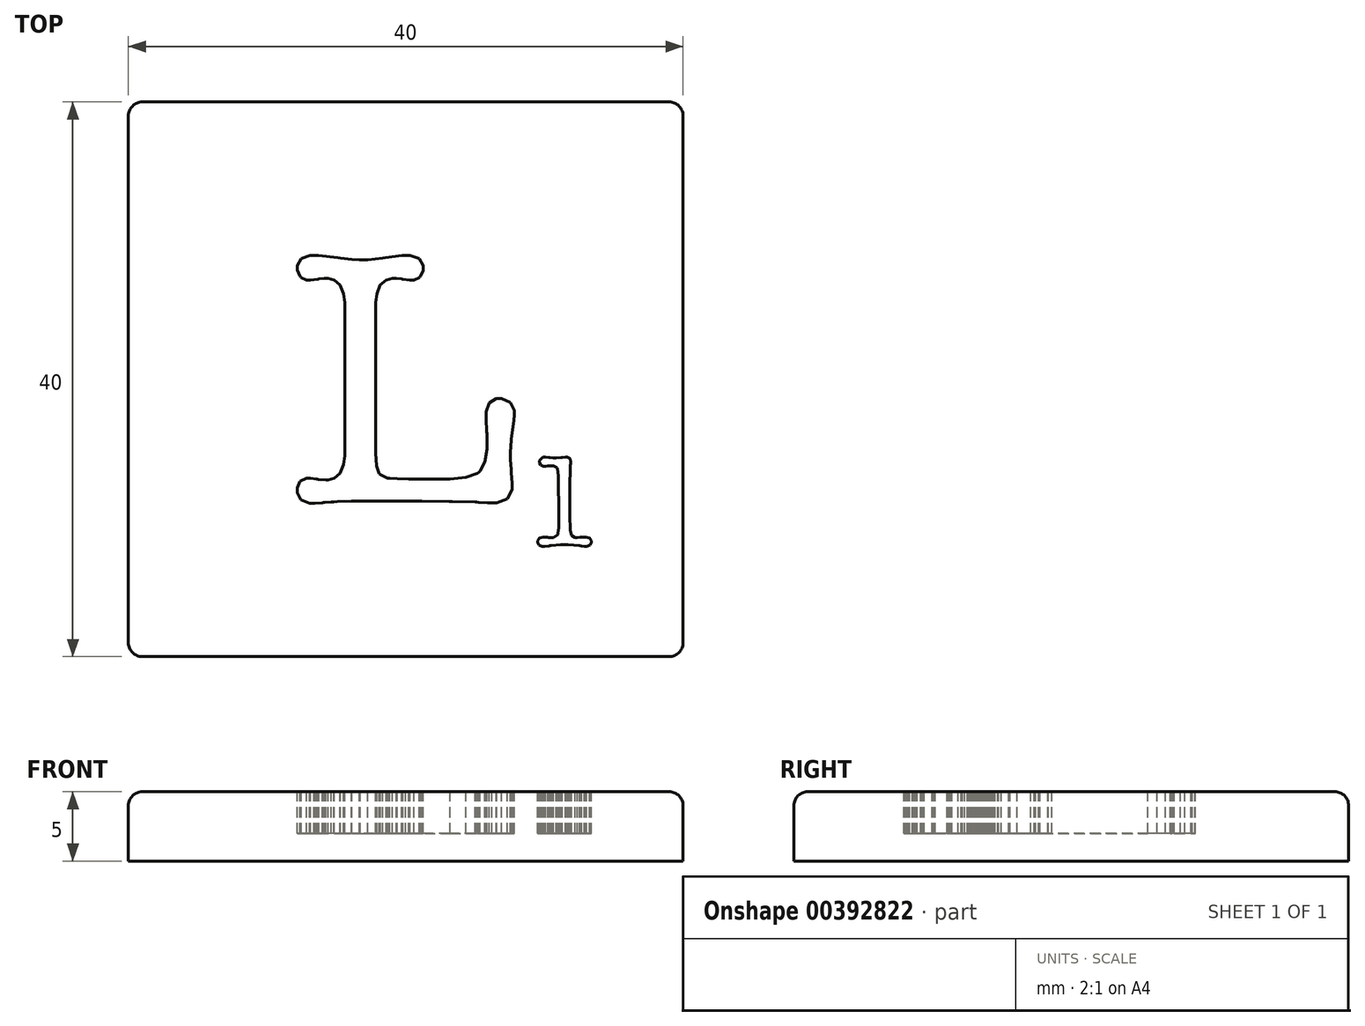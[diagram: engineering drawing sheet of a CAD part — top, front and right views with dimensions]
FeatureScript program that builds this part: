
annotation { "Feature Type Name" : "Feature", "Feature Type Description" : "" }
export const myFeature = defineFeature(function(context is Context, id is Id, definition is map)
    precondition{}
    {
        {
            var Q0;
            Q0=qCreatedBy(makeId("Top.planeOp"),FACE);
            var sketch = newSketch(context, id + "F0", { "sketchPlane" : qUnion([Q0])});
            skLineSegment(sketch, "E0.bottom", {"start": v(20, -20) * mm, "end": v(-20, -20) * mm});
            skLineSegment(sketch, "E0.top", {"start": v(20, 20) * mm, "end": v(-20, 20) * mm});
            skLineSegment(sketch, "E0.left", {"start": v(20, -20) * mm, "end": v(20, 20) * mm});
            skLineSegment(sketch, "E0.right", {"start": v(-20, -20) * mm, "end": v(-20, 20) * mm});
            skPoint(sketch, "E0.middle", {"position": v(0, 0) * mm});
            skSolve(sketch);
        }
        {
            var Q0;
            Q0=makeQuery(id+"F0.imprint","IMPRINT",FACE,{"disambiguationData":[TD([[makeQuery(id+"F0.imprint","IMPRINT",EDGE,{"derivedFrom":sQuery(id+"F0.wireOp",EDGE,"E0.bottom")}),-1.0]])]});
            extrude(context, id + "F1", {"entities" : qUnion([Q0]), "depth" : -5 * mm});
        }
        {
            var Q0;
            Q0=makeQuery(id+"F1.opExtrude","CAP_FACE",FACE,{"disambiguationData":[OSD([sQuery(id+"F0.wireOp",EDGE,"E0.bottom"),sQuery(id+"F0.wireOp",EDGE,"E0.top"),sQuery(id+"F0.wireOp",EDGE,"E0.left"),sQuery(id+"F0.wireOp",EDGE,"E0.right")])],"isStart":true});
            var Q1;
            Q1=makeQuery(id+"F1.opExtrude","SWEPT_EDGE",EDGE,{"disambiguationData":[OSD([sQuery(id+"F0.wireOp",EDGE,"E0.top"),sQuery(id+"F0.wireOp",EDGE,"E0.right")])]});
            var Q2;
            Q2=makeQuery(id+"F1.opExtrude","SWEPT_EDGE",EDGE,{"disambiguationData":[OSD([sQuery(id+"F0.wireOp",EDGE,"E0.top"),sQuery(id+"F0.wireOp",EDGE,"E0.left")])]});
            var Q3;
            Q3=makeQuery(id+"F1.opExtrude","SWEPT_EDGE",EDGE,{"disambiguationData":[OSD([sQuery(id+"F0.wireOp",EDGE,"E0.bottom"),sQuery(id+"F0.wireOp",EDGE,"E0.right")])]});
            var Q4;
            Q4=makeQuery(id+"F1.opExtrude","SWEPT_EDGE",EDGE,{"disambiguationData":[OSD([sQuery(id+"F0.wireOp",EDGE,"E0.bottom"),sQuery(id+"F0.wireOp",EDGE,"E0.left")])]});
            fillet(context, id + "F2", {"entities" : qUnion([Q0, Q1, Q2, Q3, Q4]), "radius" : 1 * mm, "tangentPropagation" : true, "allowEdgeOverflow" : false});
        }
        {
            var Q0;
            Q0=qCreatedBy(makeId("Top.planeOp"),FACE);
            var sketch = newSketch(context, id + "F3", { "sketchPlane" : qUnion([Q0])});
            skLineSegment(sketch, "E1", {"start": v(-2.17, -5) * mm, "end": v(-2.17, -5.31) * mm});
            skLineSegment(sketch, "E2", {"start": v(-2.17, -5.31) * mm, "end": v(-2.1, -6.24) * mm});
            skLineSegment(sketch, "E3", {"start": v(-2.1, -6.24) * mm, "end": v(-1.9, -6.8) * mm});
            skLineSegment(sketch, "E4", {"start": v(-1.9, -6.8) * mm, "end": v(-1.85, -6.85) * mm});
            skLineSegment(sketch, "E5", {"start": v(-1.85, -6.85) * mm, "end": v(-1.81, -6.9) * mm});
            skLineSegment(sketch, "E6", {"start": v(-1.81, -6.9) * mm, "end": v(-1.3, -7.13) * mm});
            skLineSegment(sketch, "E7", {"start": v(-1.3, -7.13) * mm, "end": v(-1.23, -7.14) * mm});
            skLineSegment(sketch, "E8", {"start": v(-1.23, -7.14) * mm, "end": v(-1.17, -7.15) * mm});
            skLineSegment(sketch, "E9", {"start": v(-1.17, -7.15) * mm, "end": v(-0.6, -7.18) * mm});
            skLineSegment(sketch, "E10", {"start": v(-0.6, -7.18) * mm, "end": v(0.22, -7.2) * mm});
            skLineSegment(sketch, "E11", {"start": v(0.22, -7.2) * mm, "end": v(0.5, -7.2) * mm});
            skLineSegment(sketch, "E12", {"start": v(0.5, -7.2) * mm, "end": v(2.83, -7.2) * mm});
            skLineSegment(sketch, "E13", {"start": v(2.83, -7.2) * mm, "end": v(3.21, -7.2) * mm});
            skLineSegment(sketch, "E14", {"start": v(3.21, -7.2) * mm, "end": v(4.35, -7.07) * mm});
            skLineSegment(sketch, "E15", {"start": v(4.35, -7.07) * mm, "end": v(5.16, -6.79) * mm});
            skLineSegment(sketch, "E16", {"start": v(5.16, -6.79) * mm, "end": v(5.27, -6.7) * mm});
            skLineSegment(sketch, "E17", {"start": v(5.27, -6.7) * mm, "end": v(5.37, -6.62) * mm});
            skLineSegment(sketch, "E18", {"start": v(5.37, -6.62) * mm, "end": v(5.72, -5.97) * mm});
            skLineSegment(sketch, "E19", {"start": v(5.72, -5.97) * mm, "end": v(5.87, -5.04) * mm});
            skLineSegment(sketch, "E20", {"start": v(5.87, -5.04) * mm, "end": v(5.87, -4.74) * mm});
            skLineSegment(sketch, "E21", {"start": v(5.87, -4.74) * mm, "end": v(5.87, -4.5) * mm});
            skLineSegment(sketch, "E22", {"start": v(5.87, -4.5) * mm, "end": v(5.85, -3.9) * mm});
            skLineSegment(sketch, "E23", {"start": v(5.85, -3.9) * mm, "end": v(5.85, -3.8) * mm});
            skLineSegment(sketch, "E24", {"start": v(5.85, -3.8) * mm, "end": v(5.84, -3.64) * mm});
            skLineSegment(sketch, "E25", {"start": v(5.84, -3.64) * mm, "end": v(5.8, -2.98) * mm});
            skLineSegment(sketch, "E26", {"start": v(5.8, -2.98) * mm, "end": v(5.8, -2.67) * mm});
            skLineSegment(sketch, "E27", {"start": v(5.8, -2.67) * mm, "end": v(5.8, -2.57) * mm});
            skLineSegment(sketch, "E28", {"start": v(5.8, -2.57) * mm, "end": v(5.8, -2.35) * mm});
            skLineSegment(sketch, "E29", {"start": v(5.8, -2.35) * mm, "end": v(6.03, -1.7) * mm});
            skLineSegment(sketch, "E30", {"start": v(6.03, -1.7) * mm, "end": v(6.55, -1.4) * mm});
            skLineSegment(sketch, "E31", {"start": v(6.55, -1.4) * mm, "end": v(6.72, -1.4) * mm});
            skLineSegment(sketch, "E32", {"start": v(6.72, -1.4) * mm, "end": v(6.93, -1.4) * mm});
            skLineSegment(sketch, "E33", {"start": v(6.93, -1.4) * mm, "end": v(7.55, -1.67) * mm});
            skLineSegment(sketch, "E34", {"start": v(7.55, -1.67) * mm, "end": v(7.83, -2.26) * mm});
            skLineSegment(sketch, "E35", {"start": v(7.83, -2.26) * mm, "end": v(7.83, -2.46) * mm});
            skLineSegment(sketch, "E36", {"start": v(7.83, -2.46) * mm, "end": v(7.83, -2.59) * mm});
            skLineSegment(sketch, "E37", {"start": v(7.83, -2.59) * mm, "end": v(7.8, -2.93) * mm});
            skLineSegment(sketch, "E38", {"start": v(7.8, -2.93) * mm, "end": v(7.8, -2.96) * mm});
            skLineSegment(sketch, "E39", {"start": v(7.8, -2.96) * mm, "end": v(7.62, -4.31) * mm});
            skLineSegment(sketch, "E40", {"start": v(7.62, -4.31) * mm, "end": v(7.6, -4.4) * mm});
            skLineSegment(sketch, "E41", {"start": v(7.6, -4.4) * mm, "end": v(7.54, -5.25) * mm});
            skLineSegment(sketch, "E42", {"start": v(7.54, -5.25) * mm, "end": v(7.54, -5.53) * mm});
            skLineSegment(sketch, "E43", {"start": v(7.54, -5.53) * mm, "end": v(7.54, -5.8) * mm});
            skLineSegment(sketch, "E44", {"start": v(7.54, -5.8) * mm, "end": v(7.6, -6.5) * mm});
            skLineSegment(sketch, "E45", {"start": v(7.6, -6.5) * mm, "end": v(7.6, -6.63) * mm});
            skLineSegment(sketch, "E46", {"start": v(7.6, -6.63) * mm, "end": v(7.62, -6.75) * mm});
            skLineSegment(sketch, "E47", {"start": v(7.62, -6.75) * mm, "end": v(7.67, -7.48) * mm});
            skLineSegment(sketch, "E48", {"start": v(7.67, -7.48) * mm, "end": v(7.67, -7.73) * mm});
            skLineSegment(sketch, "E49", {"start": v(7.67, -7.73) * mm, "end": v(7.67, -7.95) * mm});
            skLineSegment(sketch, "E50", {"start": v(7.67, -7.95) * mm, "end": v(7.34, -8.62) * mm});
            skLineSegment(sketch, "E51", {"start": v(7.34, -8.62) * mm, "end": v(6.58, -8.92) * mm});
            skLineSegment(sketch, "E52", {"start": v(6.58, -8.92) * mm, "end": v(6.32, -8.92) * mm});
            skLineSegment(sketch, "E53", {"start": v(6.32, -8.92) * mm, "end": v(6.21, -8.92) * mm});
            skLineSegment(sketch, "E54", {"start": v(6.21, -8.92) * mm, "end": v(5.89, -8.9) * mm});
            skLineSegment(sketch, "E55", {"start": v(5.89, -8.9) * mm, "end": v(5.27, -8.87) * mm});
            skLineSegment(sketch, "E56", {"start": v(5.27, -8.87) * mm, "end": v(5.1, -8.86) * mm});
            skLineSegment(sketch, "E57", {"start": v(5.1, -8.86) * mm, "end": v(5, -8.86) * mm});
            skLineSegment(sketch, "E58", {"start": v(5, -8.86) * mm, "end": v(3.37, -8.81) * mm});
            skLineSegment(sketch, "E59", {"start": v(3.37, -8.81) * mm, "end": v(3.15, -8.81) * mm});
            skLineSegment(sketch, "E60", {"start": v(3.15, -8.81) * mm, "end": v(1.16, -8.78) * mm});
            skLineSegment(sketch, "E61", {"start": v(1.16, -8.78) * mm, "end": v(-3.07, -8.78) * mm});
            skLineSegment(sketch, "E62", {"start": v(-3.07, -8.78) * mm, "end": v(-3.28, -8.78) * mm});
            skLineSegment(sketch, "E63", {"start": v(-3.28, -8.78) * mm, "end": v(-3.92, -8.8) * mm});
            skLineSegment(sketch, "E64", {"start": v(-3.92, -8.8) * mm, "end": v(-4.94, -8.83) * mm});
            skLineSegment(sketch, "E65", {"start": v(-4.94, -8.83) * mm, "end": v(-5.19, -8.84) * mm});
            skLineSegment(sketch, "E66", {"start": v(-5.19, -8.84) * mm, "end": v(-5.37, -8.84) * mm});
            skLineSegment(sketch, "E67", {"start": v(-5.37, -8.84) * mm, "end": v(-5.83, -8.88) * mm});
            skLineSegment(sketch, "E68", {"start": v(-5.83, -8.88) * mm, "end": v(-5.91, -8.9) * mm});
            skLineSegment(sketch, "E69", {"start": v(-5.91, -8.9) * mm, "end": v(-6, -8.9) * mm});
            skLineSegment(sketch, "E70", {"start": v(-6, -8.9) * mm, "end": v(-6.54, -8.94) * mm});
            skLineSegment(sketch, "E71", {"start": v(-6.54, -8.94) * mm, "end": v(-6.72, -8.94) * mm});
            skLineSegment(sketch, "E72", {"start": v(-6.72, -8.94) * mm, "end": v(-6.93, -8.94) * mm});
            skLineSegment(sketch, "E73", {"start": v(-6.93, -8.94) * mm, "end": v(-7.55, -8.7) * mm});
            skLineSegment(sketch, "E74", {"start": v(-7.55, -8.7) * mm, "end": v(-7.83, -8.17) * mm});
            skLineSegment(sketch, "E75", {"start": v(-7.83, -8.17) * mm, "end": v(-7.83, -8) * mm});
            skLineSegment(sketch, "E76", {"start": v(-7.83, -8) * mm, "end": v(-7.83, -7.83) * mm});
            skLineSegment(sketch, "E77", {"start": v(-7.83, -7.83) * mm, "end": v(-7.63, -7.35) * mm});
            skLineSegment(sketch, "E78", {"start": v(-7.63, -7.35) * mm, "end": v(-7.17, -7.14) * mm});
            skLineSegment(sketch, "E79", {"start": v(-7.17, -7.14) * mm, "end": v(-7.01, -7.14) * mm});
            skLineSegment(sketch, "E80", {"start": v(-7.01, -7.14) * mm, "end": v(-6.85, -7.14) * mm});
            skLineSegment(sketch, "E81", {"start": v(-6.85, -7.14) * mm, "end": v(-6.45, -7.2) * mm});
            skLineSegment(sketch, "E82", {"start": v(-6.45, -7.2) * mm, "end": v(-6.38, -7.2) * mm});
            skLineSegment(sketch, "E83", {"start": v(-6.38, -7.2) * mm, "end": v(-6.3, -7.22) * mm});
            skLineSegment(sketch, "E84", {"start": v(-6.3, -7.22) * mm, "end": v(-5.74, -7.28) * mm});
            skLineSegment(sketch, "E85", {"start": v(-5.74, -7.28) * mm, "end": v(-5.6, -7.28) * mm});
            skLineSegment(sketch, "E86", {"start": v(-5.6, -7.28) * mm, "end": v(-5.15, -7.15) * mm});
            skLineSegment(sketch, "E87", {"start": v(-5.15, -7.15) * mm, "end": v(-4.73, -6.78) * mm});
            skLineSegment(sketch, "E88", {"start": v(-4.73, -6.78) * mm, "end": v(-4.48, -6.16) * mm});
            skLineSegment(sketch, "E89", {"start": v(-4.48, -6.16) * mm, "end": v(-4.4, -5.5) * mm});
            skLineSegment(sketch, "E90", {"start": v(-4.4, -5.5) * mm, "end": v(-4.4, -5.3) * mm});
            skLineSegment(sketch, "E91", {"start": v(-4.4, -5.3) * mm, "end": v(-4.4, 5.32) * mm});
            skLineSegment(sketch, "E92", {"start": v(-4.4, 5.32) * mm, "end": v(-4.4, 5.53) * mm});
            skLineSegment(sketch, "E93", {"start": v(-4.4, 5.53) * mm, "end": v(-4.48, 6.18) * mm});
            skLineSegment(sketch, "E94", {"start": v(-4.48, 6.18) * mm, "end": v(-4.73, 6.79) * mm});
            skLineSegment(sketch, "E95", {"start": v(-4.73, 6.79) * mm, "end": v(-5.15, 7.16) * mm});
            skLineSegment(sketch, "E96", {"start": v(-5.15, 7.16) * mm, "end": v(-5.6, 7.28) * mm});
            skLineSegment(sketch, "E97", {"start": v(-5.6, 7.28) * mm, "end": v(-5.74, 7.28) * mm});
            skLineSegment(sketch, "E98", {"start": v(-5.74, 7.28) * mm, "end": v(-5.88, 7.28) * mm});
            skLineSegment(sketch, "E99", {"start": v(-5.88, 7.28) * mm, "end": v(-6.27, 7.23) * mm});
            skLineSegment(sketch, "E100", {"start": v(-6.27, 7.23) * mm, "end": v(-6.3, 7.22) * mm});
            skLineSegment(sketch, "E101", {"start": v(-6.3, 7.22) * mm, "end": v(-6.37, 7.21) * mm});
            skLineSegment(sketch, "E102", {"start": v(-6.37, 7.21) * mm, "end": v(-6.85, 7.14) * mm});
            skLineSegment(sketch, "E103", {"start": v(-6.85, 7.14) * mm, "end": v(-7.01, 7.14) * mm});
            skLineSegment(sketch, "E104", {"start": v(-7.01, 7.14) * mm, "end": v(-7.16, 7.14) * mm});
            skLineSegment(sketch, "E105", {"start": v(-7.16, 7.14) * mm, "end": v(-7.55, 7.35) * mm});
            skLineSegment(sketch, "E106", {"start": v(-7.55, 7.35) * mm, "end": v(-7.6, 7.4) * mm});
            skLineSegment(sketch, "E107", {"start": v(-7.6, 7.4) * mm, "end": v(-7.63, 7.44) * mm});
            skLineSegment(sketch, "E108", {"start": v(-7.63, 7.44) * mm, "end": v(-7.83, 7.87) * mm});
            skLineSegment(sketch, "E109", {"start": v(-7.83, 7.87) * mm, "end": v(-7.83, 8.02) * mm});
            skLineSegment(sketch, "E110", {"start": v(-7.83, 8.02) * mm, "end": v(-7.83, 8.2) * mm});
            skLineSegment(sketch, "E111", {"start": v(-7.83, 8.2) * mm, "end": v(-7.55, 8.71) * mm});
            skLineSegment(sketch, "E112", {"start": v(-7.55, 8.71) * mm, "end": v(-6.9, 8.94) * mm});
            skLineSegment(sketch, "E113", {"start": v(-6.9, 8.94) * mm, "end": v(-6.7, 8.94) * mm});
            skLineSegment(sketch, "E114", {"start": v(-6.7, 8.94) * mm, "end": v(-6.6, 8.94) * mm});
            skLineSegment(sketch, "E115", {"start": v(-6.6, 8.94) * mm, "end": v(-6.34, 8.92) * mm});
            skLineSegment(sketch, "E116", {"start": v(-6.34, 8.92) * mm, "end": v(-6.3, 8.92) * mm});
            skLineSegment(sketch, "E117", {"start": v(-6.3, 8.92) * mm, "end": v(-4.9, 8.76) * mm});
            skLineSegment(sketch, "E118", {"start": v(-4.9, 8.76) * mm, "end": v(-4.7, 8.74) * mm});
            skLineSegment(sketch, "E119", {"start": v(-4.7, 8.74) * mm, "end": v(-3.88, 8.66) * mm});
            skLineSegment(sketch, "E120", {"start": v(-3.88, 8.66) * mm, "end": v(-3.35, 8.63) * mm});
            skLineSegment(sketch, "E121", {"start": v(-3.35, 8.63) * mm, "end": v(-3.18, 8.63) * mm});
            skLineSegment(sketch, "E122", {"start": v(-3.18, 8.63) * mm, "end": v(-2.75, 8.63) * mm});
            skLineSegment(sketch, "E123", {"start": v(-2.75, 8.63) * mm, "end": v(-1.65, 8.74) * mm});
            skLineSegment(sketch, "E124", {"start": v(-1.65, 8.74) * mm, "end": v(-1.48, 8.76) * mm});
            skLineSegment(sketch, "E125", {"start": v(-1.48, 8.76) * mm, "end": v(-0.26, 8.92) * mm});
            skLineSegment(sketch, "E126", {"start": v(-0.26, 8.92) * mm, "end": v(-0.23, 8.92) * mm});
            skLineSegment(sketch, "E127", {"start": v(-0.23, 8.92) * mm, "end": v(0, 8.94) * mm});
            skLineSegment(sketch, "E128", {"start": v(0, 8.94) * mm, "end": v(0.08, 8.94) * mm});
            skLineSegment(sketch, "E129", {"start": v(0.08, 8.94) * mm, "end": v(0.3, 8.94) * mm});
            skLineSegment(sketch, "E130", {"start": v(0.3, 8.94) * mm, "end": v(0.97, 8.71) * mm});
            skLineSegment(sketch, "E131", {"start": v(0.97, 8.71) * mm, "end": v(1.27, 8.2) * mm});
            skLineSegment(sketch, "E132", {"start": v(1.27, 8.2) * mm, "end": v(1.27, 8.02) * mm});
            skLineSegment(sketch, "E133", {"start": v(1.27, 8.02) * mm, "end": v(1.27, 7.86) * mm});
            skLineSegment(sketch, "E134", {"start": v(1.27, 7.86) * mm, "end": v(1.07, 7.44) * mm});
            skLineSegment(sketch, "E135", {"start": v(1.07, 7.44) * mm, "end": v(1.03, 7.4) * mm});
            skLineSegment(sketch, "E136", {"start": v(1.03, 7.4) * mm, "end": v(1, 7.35) * mm});
            skLineSegment(sketch, "E137", {"start": v(1, 7.35) * mm, "end": v(0.58, 7.14) * mm});
            skLineSegment(sketch, "E138", {"start": v(0.58, 7.14) * mm, "end": v(0.45, 7.14) * mm});
            skLineSegment(sketch, "E139", {"start": v(0.45, 7.14) * mm, "end": v(0.27, 7.14) * mm});
            skLineSegment(sketch, "E140", {"start": v(0.27, 7.14) * mm, "end": v(-0.2, 7.21) * mm});
            skLineSegment(sketch, "E141", {"start": v(-0.2, 7.21) * mm, "end": v(-0.26, 7.22) * mm});
            skLineSegment(sketch, "E142", {"start": v(-0.26, 7.22) * mm, "end": v(-0.3, 7.23) * mm});
            skLineSegment(sketch, "E143", {"start": v(-0.3, 7.23) * mm, "end": v(-0.69, 7.28) * mm});
            skLineSegment(sketch, "E144", {"start": v(-0.69, 7.28) * mm, "end": v(-0.82, 7.28) * mm});
            skLineSegment(sketch, "E145", {"start": v(-0.82, 7.28) * mm, "end": v(-0.97, 7.28) * mm});
            skLineSegment(sketch, "E146", {"start": v(-0.97, 7.28) * mm, "end": v(-1.41, 7.16) * mm});
            skLineSegment(sketch, "E147", {"start": v(-1.41, 7.16) * mm, "end": v(-1.83, 6.79) * mm});
            skLineSegment(sketch, "E148", {"start": v(-1.83, 6.79) * mm, "end": v(-2.08, 6.18) * mm});
            skLineSegment(sketch, "E149", {"start": v(-2.08, 6.18) * mm, "end": v(-2.17, 5.53) * mm});
            skLineSegment(sketch, "E150", {"start": v(-2.17, 5.53) * mm, "end": v(-2.17, 5.32) * mm});
            skLineSegment(sketch, "E151", {"start": v(-2.17, 5.32) * mm, "end": v(-2.17, -5) * mm});
            skSolve(sketch);
        }
        {
            var Q0;
            Q0=qCreatedBy(makeId("Top.planeOp"),FACE);
            var sketch = newSketch(context, id + "F4", { "sketchPlane" : qUnion([Q0])});
            skLineSegment(sketch, "E152", {"start": v(11.05, -9.8) * mm, "end": v(11.02, -7.04) * mm});
            skLineSegment(sketch, "E153", {"start": v(11.02, -7.04) * mm, "end": v(11.02, -6.96) * mm});
            skLineSegment(sketch, "E154", {"start": v(11.02, -6.96) * mm, "end": v(10.94, -6.42) * mm});
            skLineSegment(sketch, "E155", {"start": v(10.94, -6.42) * mm, "end": v(10.92, -6.4) * mm});
            skLineSegment(sketch, "E156", {"start": v(10.92, -6.4) * mm, "end": v(10.9, -6.37) * mm});
            skLineSegment(sketch, "E157", {"start": v(10.9, -6.37) * mm, "end": v(10.65, -6.23) * mm});
            skLineSegment(sketch, "E158", {"start": v(10.65, -6.23) * mm, "end": v(10.57, -6.23) * mm});
            skLineSegment(sketch, "E159", {"start": v(10.57, -6.23) * mm, "end": v(10.5, -6.23) * mm});
            skLineSegment(sketch, "E160", {"start": v(10.5, -6.23) * mm, "end": v(10.32, -6.25) * mm});
            skLineSegment(sketch, "E161", {"start": v(10.32, -6.25) * mm, "end": v(10.29, -6.26) * mm});
            skLineSegment(sketch, "E162", {"start": v(10.29, -6.26) * mm, "end": v(10.26, -6.26) * mm});
            skLineSegment(sketch, "E163", {"start": v(10.26, -6.26) * mm, "end": v(10.07, -6.28) * mm});
            skLineSegment(sketch, "E164", {"start": v(10.07, -6.28) * mm, "end": v(10.01, -6.28) * mm});
            skLineSegment(sketch, "E165", {"start": v(10.01, -6.28) * mm, "end": v(9.94, -6.28) * mm});
            skLineSegment(sketch, "E166", {"start": v(9.94, -6.28) * mm, "end": v(9.73, -6.2) * mm});
            skLineSegment(sketch, "E167", {"start": v(9.73, -6.2) * mm, "end": v(9.64, -6.01) * mm});
            skLineSegment(sketch, "E168", {"start": v(9.64, -6.01) * mm, "end": v(9.64, -5.95) * mm});
            skLineSegment(sketch, "E169", {"start": v(9.64, -5.95) * mm, "end": v(9.64, -5.86) * mm});
            skLineSegment(sketch, "E170", {"start": v(9.64, -5.86) * mm, "end": v(9.9, -5.61) * mm});
            skLineSegment(sketch, "E171", {"start": v(9.9, -5.61) * mm, "end": v(10, -5.61) * mm});
            skLineSegment(sketch, "E172", {"start": v(10, -5.61) * mm, "end": v(10.08, -5.61) * mm});
            skLineSegment(sketch, "E173", {"start": v(10.08, -5.61) * mm, "end": v(10.31, -5.63) * mm});
            skLineSegment(sketch, "E174", {"start": v(10.31, -5.63) * mm, "end": v(10.35, -5.64) * mm});
            skLineSegment(sketch, "E175", {"start": v(10.35, -5.64) * mm, "end": v(10.4, -5.64) * mm});
            skLineSegment(sketch, "E176", {"start": v(10.4, -5.64) * mm, "end": v(10.64, -5.66) * mm});
            skLineSegment(sketch, "E177", {"start": v(10.64, -5.66) * mm, "end": v(10.73, -5.66) * mm});
            skLineSegment(sketch, "E178", {"start": v(10.73, -5.66) * mm, "end": v(10.85, -5.66) * mm});
            skLineSegment(sketch, "E179", {"start": v(10.85, -5.66) * mm, "end": v(11.2, -5.65) * mm});
            skLineSegment(sketch, "E180", {"start": v(11.2, -5.65) * mm, "end": v(11.23, -5.64) * mm});
            skLineSegment(sketch, "E181", {"start": v(11.23, -5.64) * mm, "end": v(11.28, -5.64) * mm});
            skLineSegment(sketch, "E182", {"start": v(11.28, -5.64) * mm, "end": v(11.52, -5.61) * mm});
            skLineSegment(sketch, "E183", {"start": v(11.52, -5.61) * mm, "end": v(11.6, -5.61) * mm});
            skLineSegment(sketch, "E184", {"start": v(11.6, -5.61) * mm, "end": v(11.66, -5.61) * mm});
            skLineSegment(sketch, "E185", {"start": v(11.66, -5.61) * mm, "end": v(11.84, -5.72) * mm});
            skLineSegment(sketch, "E186", {"start": v(11.84, -5.72) * mm, "end": v(11.85, -5.74) * mm});
            skLineSegment(sketch, "E187", {"start": v(11.85, -5.74) * mm, "end": v(11.86, -5.75) * mm});
            skLineSegment(sketch, "E188", {"start": v(11.86, -5.75) * mm, "end": v(11.89, -5.96) * mm});
            skLineSegment(sketch, "E189", {"start": v(11.89, -5.96) * mm, "end": v(11.89, -6.03) * mm});
            skLineSegment(sketch, "E190", {"start": v(11.89, -6.03) * mm, "end": v(11.89, -6.1) * mm});
            skLineSegment(sketch, "E191", {"start": v(11.89, -6.1) * mm, "end": v(11.88, -6.23) * mm});
            skLineSegment(sketch, "E192", {"start": v(11.88, -6.23) * mm, "end": v(11.88, -6.26) * mm});
            skLineSegment(sketch, "E193", {"start": v(11.88, -6.26) * mm, "end": v(11.87, -6.43) * mm});
            skLineSegment(sketch, "E194", {"start": v(11.87, -6.43) * mm, "end": v(11.83, -7.69) * mm});
            skLineSegment(sketch, "E195", {"start": v(11.83, -7.69) * mm, "end": v(11.83, -8.11) * mm});
            skLineSegment(sketch, "E196", {"start": v(11.83, -8.11) * mm, "end": v(11.83, -9.19) * mm});
            skLineSegment(sketch, "E197", {"start": v(11.83, -9.19) * mm, "end": v(11.84, -9.9) * mm});
            skLineSegment(sketch, "E198", {"start": v(11.84, -9.9) * mm, "end": v(11.84, -9.98) * mm});
            skLineSegment(sketch, "E199", {"start": v(11.84, -9.98) * mm, "end": v(11.85, -10.08) * mm});
            skLineSegment(sketch, "E200", {"start": v(11.85, -10.08) * mm, "end": v(11.86, -10.6) * mm});
            skLineSegment(sketch, "E201", {"start": v(11.86, -10.6) * mm, "end": v(11.86, -10.77) * mm});
            skLineSegment(sketch, "E202", {"start": v(11.86, -10.77) * mm, "end": v(11.86, -10.88) * mm});
            skLineSegment(sketch, "E203", {"start": v(11.86, -10.88) * mm, "end": v(11.98, -11.26) * mm});
            skLineSegment(sketch, "E204", {"start": v(11.98, -11.26) * mm, "end": v(12.22, -11.42) * mm});
            skLineSegment(sketch, "E205", {"start": v(12.22, -11.42) * mm, "end": v(12.3, -11.42) * mm});
            skLineSegment(sketch, "E206", {"start": v(12.3, -11.42) * mm, "end": v(12.38, -11.42) * mm});
            skLineSegment(sketch, "E207", {"start": v(12.38, -11.42) * mm, "end": v(12.58, -11.4) * mm});
            skLineSegment(sketch, "E208", {"start": v(12.58, -11.4) * mm, "end": v(12.61, -11.4) * mm});
            skLineSegment(sketch, "E209", {"start": v(12.61, -11.4) * mm, "end": v(12.65, -11.4) * mm});
            skLineSegment(sketch, "E210", {"start": v(12.65, -11.4) * mm, "end": v(12.93, -11.38) * mm});
            skLineSegment(sketch, "E211", {"start": v(12.93, -11.38) * mm, "end": v(13.01, -11.38) * mm});
            skLineSegment(sketch, "E212", {"start": v(13.01, -11.38) * mm, "end": v(13.27, -11.46) * mm});
            skLineSegment(sketch, "E213", {"start": v(13.27, -11.46) * mm, "end": v(13.39, -11.65) * mm});
            skLineSegment(sketch, "E214", {"start": v(13.39, -11.65) * mm, "end": v(13.39, -11.71) * mm});
            skLineSegment(sketch, "E215", {"start": v(13.39, -11.71) * mm, "end": v(13.39, -11.77) * mm});
            skLineSegment(sketch, "E216", {"start": v(13.39, -11.77) * mm, "end": v(13.28, -11.96) * mm});
            skLineSegment(sketch, "E217", {"start": v(13.28, -11.96) * mm, "end": v(13.04, -12.04) * mm});
            skLineSegment(sketch, "E218", {"start": v(13.04, -12.04) * mm, "end": v(12.97, -12.04) * mm});
            skLineSegment(sketch, "E219", {"start": v(12.97, -12.04) * mm, "end": v(12.89, -12.04) * mm});
            skLineSegment(sketch, "E220", {"start": v(12.89, -12.04) * mm, "end": v(12.68, -12.03) * mm});
            skLineSegment(sketch, "E221", {"start": v(12.68, -12.03) * mm, "end": v(12.66, -12.03) * mm});
            skLineSegment(sketch, "E222", {"start": v(12.66, -12.03) * mm, "end": v(12.53, -12) * mm});
            skLineSegment(sketch, "E223", {"start": v(12.53, -12) * mm, "end": v(11.71, -11.92) * mm});
            skLineSegment(sketch, "E224", {"start": v(11.71, -11.92) * mm, "end": v(11.44, -11.92) * mm});
            skLineSegment(sketch, "E225", {"start": v(11.44, -11.92) * mm, "end": v(11.18, -11.92) * mm});
            skLineSegment(sketch, "E226", {"start": v(11.18, -11.92) * mm, "end": v(10.51, -12) * mm});
            skLineSegment(sketch, "E227", {"start": v(10.51, -12) * mm, "end": v(10.41, -12) * mm});
            skLineSegment(sketch, "E228", {"start": v(10.41, -12) * mm, "end": v(10.36, -12.01) * mm});
            skLineSegment(sketch, "E229", {"start": v(10.36, -12.01) * mm, "end": v(10.03, -12.05) * mm});
            skLineSegment(sketch, "E230", {"start": v(10.03, -12.05) * mm, "end": v(9.93, -12.05) * mm});
            skLineSegment(sketch, "E231", {"start": v(9.93, -12.05) * mm, "end": v(9.85, -12.05) * mm});
            skLineSegment(sketch, "E232", {"start": v(9.85, -12.05) * mm, "end": v(9.62, -11.97) * mm});
            skLineSegment(sketch, "E233", {"start": v(9.62, -11.97) * mm, "end": v(9.52, -11.77) * mm});
            skLineSegment(sketch, "E234", {"start": v(9.52, -11.77) * mm, "end": v(9.52, -11.71) * mm});
            skLineSegment(sketch, "E235", {"start": v(9.52, -11.71) * mm, "end": v(9.52, -11.65) * mm});
            skLineSegment(sketch, "E236", {"start": v(9.52, -11.65) * mm, "end": v(9.63, -11.46) * mm});
            skLineSegment(sketch, "E237", {"start": v(9.63, -11.46) * mm, "end": v(9.9, -11.38) * mm});
            skLineSegment(sketch, "E238", {"start": v(9.9, -11.38) * mm, "end": v(9.99, -11.38) * mm});
            skLineSegment(sketch, "E239", {"start": v(9.99, -11.38) * mm, "end": v(10.06, -11.38) * mm});
            skLineSegment(sketch, "E240", {"start": v(10.06, -11.38) * mm, "end": v(10.25, -11.4) * mm});
            skLineSegment(sketch, "E241", {"start": v(10.25, -11.4) * mm, "end": v(10.28, -11.4) * mm});
            skLineSegment(sketch, "E242", {"start": v(10.28, -11.4) * mm, "end": v(10.32, -11.4) * mm});
            skLineSegment(sketch, "E243", {"start": v(10.32, -11.4) * mm, "end": v(10.5, -11.42) * mm});
            skLineSegment(sketch, "E244", {"start": v(10.5, -11.42) * mm, "end": v(10.57, -11.42) * mm});
            skLineSegment(sketch, "E245", {"start": v(10.57, -11.42) * mm, "end": v(10.67, -11.42) * mm});
            skLineSegment(sketch, "E246", {"start": v(10.67, -11.42) * mm, "end": v(10.96, -11.2) * mm});
            skLineSegment(sketch, "E247", {"start": v(10.96, -11.2) * mm, "end": v(10.98, -11.16) * mm});
            skLineSegment(sketch, "E248", {"start": v(10.98, -11.16) * mm, "end": v(10.99, -11.12) * mm});
            skLineSegment(sketch, "E249", {"start": v(10.99, -11.12) * mm, "end": v(11.03, -10.7) * mm});
            skLineSegment(sketch, "E250", {"start": v(11.03, -10.7) * mm, "end": v(11.05, -10.03) * mm});
            skLineSegment(sketch, "E251", {"start": v(11.05, -10.03) * mm, "end": v(11.05, -9.8) * mm});
            skSolve(sketch);
        }
        {
            var Q0;
            Q0=qSketchRegion(id+"F3",true);
            var Q1;
            Q1=qSketchRegion(id+"F4",true);
            extrude(context, id + "F5", {"entities" : qUnion([Q0, Q1]), "depth" : -3 * mm});
        }
    });
